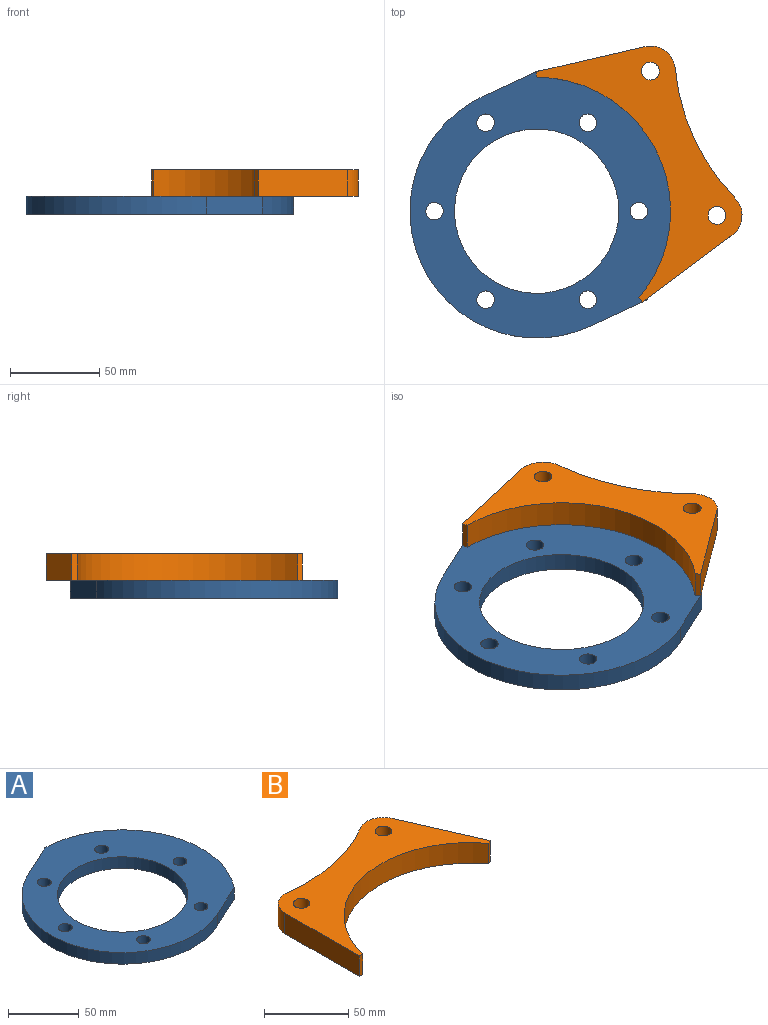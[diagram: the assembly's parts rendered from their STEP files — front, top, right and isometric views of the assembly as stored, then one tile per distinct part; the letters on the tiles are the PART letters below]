
ASSEMBLY  parts=2 mates=1
PART A: 13 faces, bbox 150x150x10 mm
  f0: plane 31.4x14.64mm, normal (0.42,-0.91,0), area 346.4mm2, adj f1,f10,f11,f12
  f1: cylinder r=79mm len=128.7mm, axis (0,0,-1), area 1764.7mm2, adj f0,f2,f11,f12
  f2: plane 31.4x14.64mm, normal (-0.42,0.91,0), area 346.4mm2, adj f1,f10,f11,f12
  f3: cylinder r=46mm len=92mm, axis (0,0,-1), area 2890.3mm2, adj f11,f12
  f4: cylinder r=4.9mm len=10mm, axis (0,0,-1), area 307.9mm2, adj f11,f12
  f5: cylinder r=4.9mm len=10mm, axis (0,0,-1), area 307.9mm2, adj f11,f12
  f6: cylinder r=4.9mm len=10mm, axis (0,0,-1), area 307.9mm2, adj f11,f12
  f7: cylinder r=4.9mm len=10mm, axis (0,0,-1), area 307.9mm2, adj f11,f12
  f8: cylinder r=4.9mm len=10mm, axis (0,0,-1), area 307.9mm2, adj f11,f12
  f9: cylinder r=4.9mm len=10mm, axis (0,0,-1), area 307.9mm2, adj f11,f12
  f10: cylinder r=71mm len=135.35mm, axis (0,0,-1), area 2230.5mm2, adj f0,f2,f11,f12
  f11: plane 150x149.99mm, normal (0,0,1), area 10248.1mm2, adj f0,f1,f2,f3,f4,f5,f6,f7
  f12: plane 150x149.99mm, normal (0,0,-1), area 10248.1mm2, adj f0,f1,f2,f3,f4,f5,f6,f7
PART B: 12 faces, bbox 139x94.8x15 mm
  f0: cylinder r=120mm len=78.02mm, axis (0,0,-1), area 1218.7mm2, adj f1,f9,f10,f11
  f1: cylinder r=14mm len=15.85mm, axis (0,0,-1), area 357.7mm2, adj f0,f2,f10,f11
  f2: plane 62.56x15mm, normal (-1,0,0), area 938.4mm2, adj f1,f3,f10,f11
  f3: plane 15x3.08mm, normal (0,-1,0), area 46.2mm2, adj f2,f4,f10,f11
  f4: cylinder r=75mm len=133.1mm, axis (0,0,-1), area 2553.6mm2, adj f3,f5,f10,f11
  f5: plane 15x2.82mm, normal (0.4,-0.92,0), area 46.2mm2, adj f4,f6,f10,f11
  f6: plane 57.32x25.05mm, normal (0.92,0.4,0), area 938.4mm2, adj f5,f9,f10,f11
  f7: cylinder r=5mm len=15mm, axis (0,0,-1), area 471.2mm2, adj f10,f11
  f8: cylinder r=5mm len=15mm, axis (0,0,-1), area 471.2mm2, adj f10,f11
  f9: cylinder r=14mm len=20.08mm, axis (0,0,-1), area 357.7mm2, adj f0,f6,f10,f11
  f10: plane 139x94.76mm, normal (0,0,1), area 4401.1mm2, adj f0,f1,f2,f3,f4,f5,f6,f7
  f11: plane 139x94.76mm, normal (0,0,-1), area 4401.1mm2, adj f0,f1,f2,f3,f4,f5,f6,f7
PLACE A t=(-3.95,-4,-5.05)mm fixed
PLACE B rot(axis=(0,0,-1),77deg) t=(-3.95,-4,4.95)mm
MATE fastened B.f4 <-> A.f1  axis (0,0,-1) through (-3.95,-4,4.95)mm
